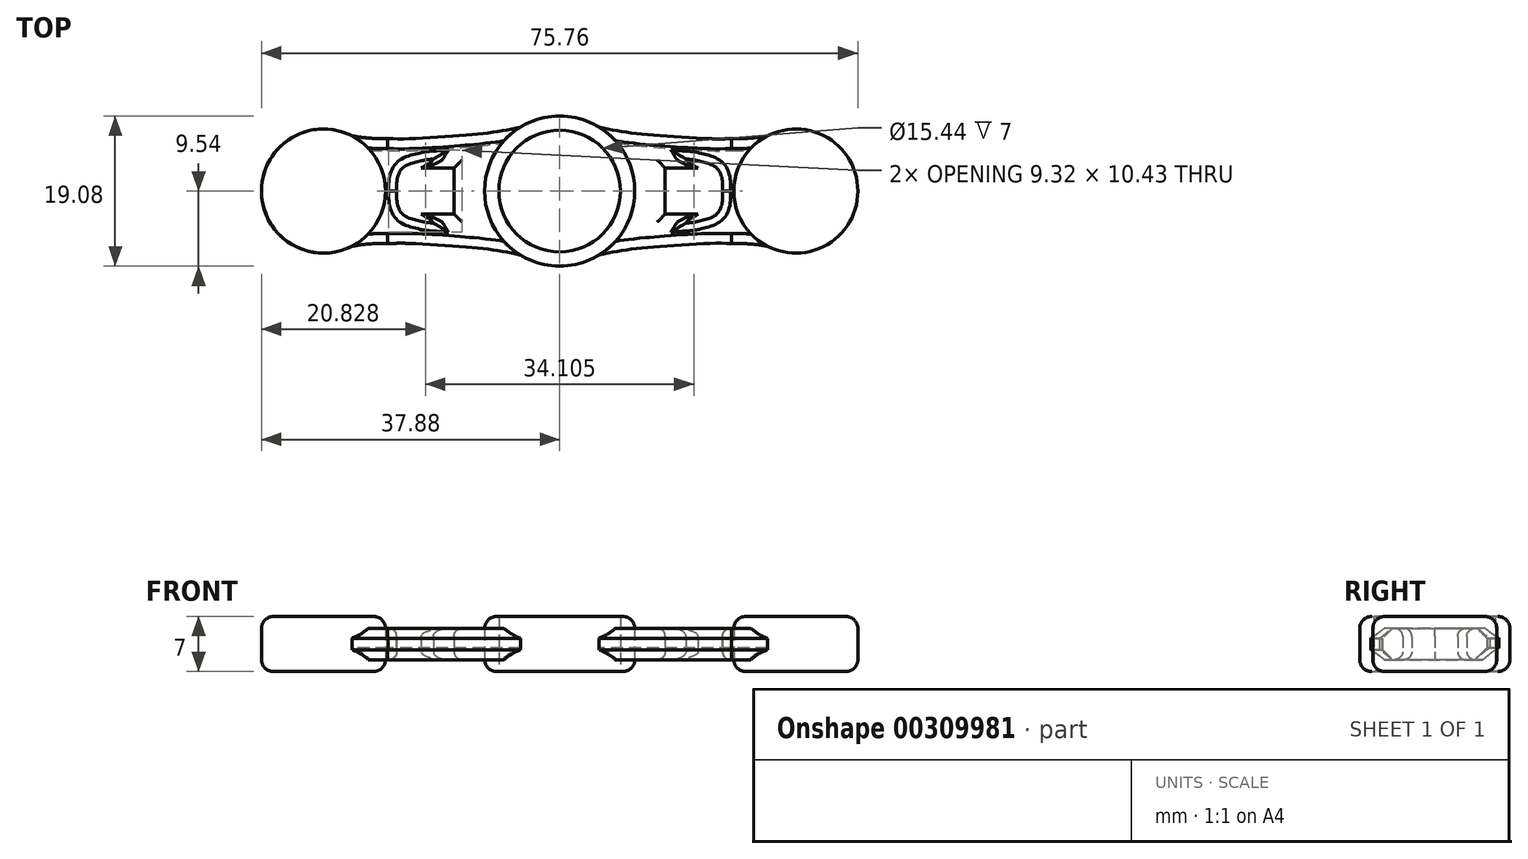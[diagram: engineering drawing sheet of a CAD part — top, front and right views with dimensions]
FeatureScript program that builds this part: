
annotation { "Feature Type Name" : "Feature", "Feature Type Description" : "" }
export const myFeature = defineFeature(function(context is Context, id is Id, definition is map)
    precondition{}
    {
        {
            var Q0;
            Q0=qCreatedBy(makeId("Top.planeOp"),FACE);
            var sketch = newSketch(context, id + "F0", { "sketchPlane" : qUnion([Q0])});
            skLineSegment(sketch, "E0.bottom", {"start": v(-38.2, 12.73) * mm, "end": v(38.2, 12.73) * mm});
            skLineSegment(sketch, "E0.top", {"start": v(-38.2, -12.73) * mm, "end": v(38.2, -12.73) * mm});
            skLineSegment(sketch, "E0.left", {"start": v(-38.2, 12.73) * mm, "end": v(-38.2, -12.73) * mm});
            skLineSegment(sketch, "E0.right", {"start": v(38.2, 12.73) * mm, "end": v(38.2, -12.73) * mm});
            skPoint(sketch, "E0.middle", {"position": v(0, 0) * mm});
            skCircle(sketch, "E1", {"center": v(0, 0) * mm, "radius": 7.72 * mm});
            skLineSegment(sketch, "E2", {"start": v(0, 12.73) * mm, "end": v(0, -12.73) * mm});
            skCircle(sketch, "E3", {"center": v(0, 0) * mm, "radius": 9.54 * mm});
            skFitSpline(sketch, "E4", {"points": [v(4.98, 8.14) * mm, v(7.16, 7.67) * mm, v(9.55, 7.33) * mm, v(13.3, 7) * mm, v(18.75, 6.65) * mm, v(21.82, 6.65) * mm], "startDerivative": vector(13.26, -2.94) * mm, "endDerivative": vector(14.49, 0.3) * mm});
            skFitSpline(sketch, "E5.MirrorCS", {"points": [v(4.98, -8.14) * mm, v(7.16, -7.67) * mm, v(9.55, -7.33) * mm, v(13.3, -7) * mm, v(18.75, -6.65) * mm, v(21.82, -6.65) * mm], "startDerivative": vector(13.26, 2.94) * mm, "endDerivative": vector(14.49, -0.3) * mm});
            skFitSpline(sketch, "E6.MirrorCS", {"points": [v(-4.98, 8.14) * mm, v(-7.16, 7.67) * mm, v(-9.55, 7.33) * mm, v(-13.3, 7) * mm, v(-18.75, 6.65) * mm, v(-21.82, 6.65) * mm], "startDerivative": vector(-13.26, -2.94) * mm, "endDerivative": vector(-14.49, 0.3) * mm});
            skFitSpline(sketch, "E7.MirrorCS", {"points": [v(-4.98, -8.14) * mm, v(-7.16, -7.67) * mm, v(-9.55, -7.33) * mm, v(-13.3, -7) * mm, v(-18.75, -6.65) * mm, v(-21.82, -6.65) * mm], "startDerivative": vector(-13.26, 2.94) * mm, "endDerivative": vector(-14.49, -0.3) * mm});
            skCircle(sketch, "E8", {"center": v(30, 0) * mm, "radius": 7.88 * mm});
            skLineSegment(sketch, "E9", {"start": v(38.2, 0) * mm, "end": v(-38.2, 0) * mm});
            skFitSpline(sketch, "E10", {"points": [v(21.82, 6.65) * mm, v(23.45, 6.68) * mm, v(25.2, 6.82) * mm, v(26.4, 7.01) * mm], "startDerivative": vector(4.61, 0.02) * mm, "endDerivative": vector(3.82, 0.64) * mm});
            skFitSpline(sketch, "E11.MirrorCS", {"points": [v(21.82, -6.65) * mm, v(23.45, -6.68) * mm, v(25.2, -6.82) * mm, v(26.4, -7.01) * mm], "startDerivative": vector(4.61, -0.02) * mm, "endDerivative": vector(3.82, -0.64) * mm});
            skCircle(sketch, "E12.MirrorC", {"center": v(-30, 0) * mm, "radius": 7.88 * mm});
            skFitSpline(sketch, "E13.MirrorCS", {"points": [v(-21.82, 6.65) * mm, v(-23.45, 6.68) * mm, v(-25.2, 6.82) * mm, v(-26.4, 7.01) * mm], "startDerivative": vector(-4.61, 0.02) * mm, "endDerivative": vector(-3.82, 0.64) * mm});
            skFitSpline(sketch, "E14.MirrorCS", {"points": [v(-21.82, -6.65) * mm, v(-23.45, -6.68) * mm, v(-25.2, -6.82) * mm, v(-26.4, -7.01) * mm], "startDerivative": vector(-4.61, -0.02) * mm, "endDerivative": vector(-3.82, -0.64) * mm});
            skFitSpline(sketch, "E15", {"points": [v(-20.68, 0) * mm, v(-20.68, 1.18) * mm, v(-20.38, 2.35) * mm, v(-19.72, 3.1) * mm, v(-18.7, 3.56) * mm, v(-17.5, 3.87) * mm], "startDerivative": vector(-0.27, 5.77) * mm, "endDerivative": vector(5.92, 1.32) * mm});
            skFitSpline(sketch, "E16", {"points": [v(-17.5, 3.87) * mm, v(-16.82, 4) * mm, v(-16.04, 4.07) * mm], "startDerivative": vector(1.36, 0.3) * mm, "endDerivative": vector(1.55, 0.1) * mm});
            skFitSpline(sketch, "E17", {"points": [v(-16.04, 4.07) * mm, v(-16.29, 3.75) * mm, v(-16.93, 3.32) * mm, v(-17.58, 2.92) * mm], "startDerivative": vector(-0.75, -1.2) * mm, "endDerivative": vector(-1.72, -1.06) * mm});
            skLineSegment(sketch, "E18", {"start": v(-17.58, 2.92) * mm, "end": v(-15.4, 2.92) * mm});
            skLineSegment(sketch, "E19.MirrorCS", {"start": v(-17.58, -2.92) * mm, "end": v(-15.4, -2.92) * mm});
            skFitSpline(sketch, "E20.MirrorCS", {"points": [v(-20.68, 0) * mm, v(-20.68, -1.18) * mm, v(-20.38, -2.35) * mm, v(-19.72, -3.1) * mm, v(-18.7, -3.56) * mm, v(-17.5, -3.87) * mm], "startDerivative": vector(-0.27, -5.77) * mm, "endDerivative": vector(5.92, -1.32) * mm});
            skFitSpline(sketch, "E21.MirrorCS", {"points": [v(-16.04, -4.07) * mm, v(-16.29, -3.75) * mm, v(-16.93, -3.32) * mm, v(-17.58, -2.92) * mm], "startDerivative": vector(-0.75, 1.2) * mm, "endDerivative": vector(-1.72, 1.06) * mm});
            skFitSpline(sketch, "E22.MirrorCS", {"points": [v(-17.5, -3.87) * mm, v(-16.82, -4) * mm, v(-16.04, -4.07) * mm], "startDerivative": vector(1.36, -0.3) * mm, "endDerivative": vector(1.55, -0.1) * mm});
            skFitSpline(sketch, "E23.MirrorCS", {"points": [v(20.68, 0) * mm, v(20.68, 1.18) * mm, v(20.38, 2.35) * mm, v(19.72, 3.1) * mm, v(18.7, 3.56) * mm, v(17.5, 3.87) * mm], "startDerivative": vector(0.27, 5.77) * mm, "endDerivative": vector(-5.92, 1.32) * mm});
            skFitSpline(sketch, "E24.MirrorCS", {"points": [v(17.5, 3.87) * mm, v(16.82, 4) * mm, v(16.04, 4.07) * mm], "startDerivative": vector(-1.36, 0.3) * mm, "endDerivative": vector(-1.55, 0.1) * mm});
            skFitSpline(sketch, "E25.MirrorCS", {"points": [v(16.04, 4.07) * mm, v(16.29, 3.75) * mm, v(16.93, 3.32) * mm, v(17.58, 2.92) * mm], "startDerivative": vector(0.75, -1.2) * mm, "endDerivative": vector(1.72, -1.06) * mm});
            skLineSegment(sketch, "E26.MirrorCS", {"start": v(17.58, 2.92) * mm, "end": v(15.4, 2.92) * mm});
            skLineSegment(sketch, "E27.MirrorCS", {"start": v(17.58, -2.92) * mm, "end": v(15.4, -2.92) * mm});
            skFitSpline(sketch, "E28.MirrorCS", {"points": [v(16.04, -4.07) * mm, v(16.29, -3.75) * mm, v(16.93, -3.32) * mm, v(17.58, -2.92) * mm], "startDerivative": vector(0.75, 1.2) * mm, "endDerivative": vector(1.72, 1.06) * mm});
            skFitSpline(sketch, "E29.MirrorCS", {"points": [v(17.5, -3.87) * mm, v(16.82, -4) * mm, v(16.04, -4.07) * mm], "startDerivative": vector(-1.36, -0.3) * mm, "endDerivative": vector(-1.55, -0.1) * mm});
            skFitSpline(sketch, "E30.MirrorCS", {"points": [v(20.68, 0) * mm, v(20.68, -1.18) * mm, v(20.38, -2.35) * mm, v(19.72, -3.1) * mm, v(18.7, -3.56) * mm, v(17.5, -3.87) * mm], "startDerivative": vector(0.27, -5.77) * mm, "endDerivative": vector(-5.92, -1.32) * mm});
            skLineSegment(sketch, "E31", {"start": v(-15.4, 2.92) * mm, "end": v(-13.4, 2.92) * mm});
            skLineSegment(sketch, "E32", {"start": v(-13.4, 2.92) * mm, "end": v(-13.4, 0) * mm});
            skLineSegment(sketch, "E33.MirrorCS", {"start": v(-13.4, -2.92) * mm, "end": v(-13.4, 0) * mm});
            skLineSegment(sketch, "E34.MirrorCS", {"start": v(-15.4, -2.92) * mm, "end": v(-13.4, -2.92) * mm});
            skLineSegment(sketch, "E35.MirrorCS", {"start": v(15.4, 2.92) * mm, "end": v(13.4, 2.92) * mm});
            skLineSegment(sketch, "E36.MirrorCS", {"start": v(13.4, 2.92) * mm, "end": v(13.4, 0) * mm});
            skLineSegment(sketch, "E37.MirrorCS", {"start": v(13.4, -2.92) * mm, "end": v(13.4, 0) * mm});
            skLineSegment(sketch, "E38.MirrorCS", {"start": v(15.4, -2.92) * mm, "end": v(13.4, -2.92) * mm});
            skSolve(sketch);
        }
        {
            var Q0;
            {var subQ0=sQuery(id+"F0.wireOp",EDGE,"E12.MirrorC");var subQ1=sQuery(id+"F0.wireOp",EDGE,"E9");var subQ2=makeQuery(id+"F0.imprint","INTERSECT",VERTEX,{"disambiguationData":[OD(0.0)],"derivedFrom":[subQ1,subQ0]});Q0=makeQuery(id+"F0.imprint","IMPRINT",FACE,{"disambiguationData":[TD([[makeQuery(id+"F0.imprint","IMPRINT",EDGE,{"disambiguationData":[TD([[subQ2,-1.0]])],"derivedFrom":subQ1}),-1.0]])]});}
            var Q1;
            {var subQ0=sQuery(id+"F0.wireOp",EDGE,"E12.MirrorC");var subQ1=sQuery(id+"F0.wireOp",EDGE,"E9");var subQ2=makeQuery(id+"F0.imprint","INTERSECT",VERTEX,{"disambiguationData":[OD(0.0)],"derivedFrom":[subQ1,subQ0]});Q1=makeQuery(id+"F0.imprint","IMPRINT",FACE,{"disambiguationData":[TD([[makeQuery(id+"F0.imprint","IMPRINT",EDGE,{"disambiguationData":[TD([[subQ2,-1.0]])],"derivedFrom":subQ1}),1.0]])]});}
            var Q2;
            {var subQ4=sQuery(id+"F0.wireOp",EDGE,"E9");var subQ6=sQuery(id+"F0.wireOp",EDGE,"E1");var subQ8=makeQuery(id+"F0.imprint","INTERSECT",VERTEX,{"disambiguationData":[OD(1.0)],"derivedFrom":[subQ6,subQ4]});Q2=makeQuery(id+"F0.imprint","IMPRINT",FACE,{"disambiguationData":[TD([[makeQuery(id+"F0.imprint","IMPRINT",EDGE,{"disambiguationData":[TD([[subQ8,-1.0]])],"derivedFrom":subQ6}),-1.0]])]});}
            var Q3;
            {var subQ4=sQuery(id+"F0.wireOp",EDGE,"E2");var subQ6=sQuery(id+"F0.wireOp",EDGE,"E1");var subQ7=makeQuery(id+"F0.imprint","INTERSECT",VERTEX,{"disambiguationData":[OD(0.0)],"derivedFrom":[subQ6,subQ4]});Q3=makeQuery(id+"F0.imprint","IMPRINT",FACE,{"disambiguationData":[TD([[makeQuery(id+"F0.imprint","IMPRINT",EDGE,{"disambiguationData":[TD([[subQ7,-1.0]])],"derivedFrom":subQ6}),-1.0]])]});}
            var Q4;
            {var subQ2=sQuery(id+"F0.wireOp",EDGE,"E2");var subQ4=sQuery(id+"F0.wireOp",EDGE,"E1");var subQ5=makeQuery(id+"F0.imprint","INTERSECT",VERTEX,{"disambiguationData":[OD(0.0)],"derivedFrom":[subQ4,subQ2]});Q4=makeQuery(id+"F0.imprint","IMPRINT",FACE,{"disambiguationData":[TD([[makeQuery(id+"F0.imprint","IMPRINT",EDGE,{"disambiguationData":[TD([[subQ5,1.0]])],"derivedFrom":subQ4}),-1.0]])]});}
            var Q5;
            {var subQ2=sQuery(id+"F0.wireOp",EDGE,"E9");var subQ6=sQuery(id+"F0.wireOp",EDGE,"E1");var subQ8=makeQuery(id+"F0.imprint","INTERSECT",VERTEX,{"disambiguationData":[OD(0.0)],"derivedFrom":[subQ6,subQ2]});Q5=makeQuery(id+"F0.imprint","IMPRINT",FACE,{"disambiguationData":[TD([[makeQuery(id+"F0.imprint","IMPRINT",EDGE,{"disambiguationData":[TD([[subQ8,1.0]])],"derivedFrom":subQ6}),-1.0]])]});}
            var Q6;
            {var subQ0=sQuery(id+"F0.wireOp",EDGE,"E8");var subQ1=makeQuery(id+"F0.imprint","INTERSECT",VERTEX,{"derivedFrom":[subQ0,sQuery(id+"F0.wireOp",EDGE,"E11.MirrorCS")]});Q6=makeQuery(id+"F0.imprint","IMPRINT",FACE,{"disambiguationData":[TD([[makeQuery(id+"F0.imprint","IMPRINT",EDGE,{"disambiguationData":[TD([[subQ1,1.0]])],"derivedFrom":subQ0}),1.0]])]});}
            var Q7;
            {var subQ0=sQuery(id+"F0.wireOp",EDGE,"E8");var subQ1=makeQuery(id+"F0.imprint","INTERSECT",VERTEX,{"derivedFrom":[subQ0,sQuery(id+"F0.wireOp",EDGE,"E10")]});Q7=makeQuery(id+"F0.imprint","IMPRINT",FACE,{"disambiguationData":[TD([[makeQuery(id+"F0.imprint","IMPRINT",EDGE,{"disambiguationData":[TD([[subQ1,1.0]])],"derivedFrom":subQ0}),1.0]])]});}
            extrude(context, id + "F1", {"entities" : qUnion([Q0, Q1, Q2, Q3, Q4, Q5, Q6, Q7]), "depth" : 7 * mm});
        }
        {
            var Q0;
            {var subQ4=sQuery(id+"F0.wireOp",EDGE,"E6.MirrorCS");Q0=makeQuery(id+"F0.imprint","IMPRINT",FACE,{"disambiguationData":[TD([[makeQuery(id+"F0.imprint","IMPRINT",EDGE,{"derivedFrom":subQ4}),1.0]])]});}
            var Q1;
            {var subQ5=sQuery(id+"F0.wireOp",EDGE,"E7.MirrorCS");Q1=makeQuery(id+"F0.imprint","IMPRINT",FACE,{"disambiguationData":[TD([[makeQuery(id+"F0.imprint","IMPRINT",EDGE,{"derivedFrom":subQ5}),-1.0]])]});}
            var Q2;
            {var subQ1=sQuery(id+"F0.wireOp",EDGE,"E5.MirrorCS");Q2=makeQuery(id+"F0.imprint","IMPRINT",FACE,{"disambiguationData":[TD([[makeQuery(id+"F0.imprint","IMPRINT",EDGE,{"derivedFrom":subQ1}),1.0]])]});}
            var Q3;
            {var subQ4=sQuery(id+"F0.wireOp",EDGE,"E4");Q3=makeQuery(id+"F0.imprint","IMPRINT",FACE,{"disambiguationData":[TD([[makeQuery(id+"F0.imprint","IMPRINT",EDGE,{"derivedFrom":subQ4}),-1.0]])]});}
            extrude(context, id + "F2", {"entities" : qUnion([Q0, Q1, Q2, Q3]), "depth" : 4 * mm});
        }
        {
            var Q0;
            Q0=makeQuery(id+"F2.opExtrude","SWEPT_BODY",BODY,{"disambiguationData":[OSD([sQuery(id+"F0.wireOp",EDGE,"E3"),sQuery(id+"F0.wireOp",EDGE,"E6.MirrorCS"),sQuery(id+"F0.wireOp",EDGE,"E7.MirrorCS"),sQuery(id+"F0.wireOp",EDGE,"E12.MirrorC"),sQuery(id+"F0.wireOp",EDGE,"E13.MirrorCS"),sQuery(id+"F0.wireOp",EDGE,"E14.MirrorCS"),sQuery(id+"F0.wireOp",EDGE,"E15"),sQuery(id+"F0.wireOp",EDGE,"E16"),sQuery(id+"F0.wireOp",EDGE,"E17"),sQuery(id+"F0.wireOp",EDGE,"E18"),sQuery(id+"F0.wireOp",EDGE,"E19.MirrorCS"),sQuery(id+"F0.wireOp",EDGE,"E20.MirrorCS"),sQuery(id+"F0.wireOp",EDGE,"E21.MirrorCS"),sQuery(id+"F0.wireOp",EDGE,"E22.MirrorCS"),sQuery(id+"F0.wireOp",EDGE,"E31"),sQuery(id+"F0.wireOp",EDGE,"E32"),sQuery(id+"F0.wireOp",EDGE,"E33.MirrorCS"),sQuery(id+"F0.wireOp",EDGE,"E34.MirrorCS")])]});
            transform(context, id + "F3", {"entities" : qUnion([Q0]), "transformType" : TransformType.TRANSLATION_3D, "dx" : 0 * mm, "dy" : 0 * mm, "dz" : 1 * mm, "makeCopy" : false});
        }
        {
            var Q0;
            Q0=makeQuery(id+"F2.opExtrude","SWEPT_BODY",BODY,{"disambiguationData":[OSD([sQuery(id+"F0.wireOp",EDGE,"E3"),sQuery(id+"F0.wireOp",EDGE,"E4"),sQuery(id+"F0.wireOp",EDGE,"E5.MirrorCS"),sQuery(id+"F0.wireOp",EDGE,"E8"),sQuery(id+"F0.wireOp",EDGE,"E10"),sQuery(id+"F0.wireOp",EDGE,"E11.MirrorCS"),sQuery(id+"F0.wireOp",EDGE,"E23.MirrorCS"),sQuery(id+"F0.wireOp",EDGE,"E24.MirrorCS"),sQuery(id+"F0.wireOp",EDGE,"E25.MirrorCS"),sQuery(id+"F0.wireOp",EDGE,"E26.MirrorCS"),sQuery(id+"F0.wireOp",EDGE,"E27.MirrorCS"),sQuery(id+"F0.wireOp",EDGE,"E28.MirrorCS"),sQuery(id+"F0.wireOp",EDGE,"E29.MirrorCS"),sQuery(id+"F0.wireOp",EDGE,"E30.MirrorCS"),sQuery(id+"F0.wireOp",EDGE,"E35.MirrorCS"),sQuery(id+"F0.wireOp",EDGE,"E36.MirrorCS"),sQuery(id+"F0.wireOp",EDGE,"E37.MirrorCS"),sQuery(id+"F0.wireOp",EDGE,"E38.MirrorCS")])]});
            transform(context, id + "F4", {"entities" : qUnion([Q0]), "transformType" : TransformType.TRANSLATION_3D, "dx" : 0 * mm, "dy" : 0 * mm, "dz" : 1 * mm, "makeCopy" : false});
        }
        {
            var Q0;
            Q0=makeQuery(id+"F2.opExtrude","SWEPT_BODY",BODY,{"disambiguationData":[OSD([sQuery(id+"F0.wireOp",EDGE,"E3"),sQuery(id+"F0.wireOp",EDGE,"E6.MirrorCS"),sQuery(id+"F0.wireOp",EDGE,"E7.MirrorCS"),sQuery(id+"F0.wireOp",EDGE,"E12.MirrorC"),sQuery(id+"F0.wireOp",EDGE,"E13.MirrorCS"),sQuery(id+"F0.wireOp",EDGE,"E14.MirrorCS"),sQuery(id+"F0.wireOp",EDGE,"E15"),sQuery(id+"F0.wireOp",EDGE,"E16"),sQuery(id+"F0.wireOp",EDGE,"E17"),sQuery(id+"F0.wireOp",EDGE,"E18"),sQuery(id+"F0.wireOp",EDGE,"E19.MirrorCS"),sQuery(id+"F0.wireOp",EDGE,"E20.MirrorCS"),sQuery(id+"F0.wireOp",EDGE,"E21.MirrorCS"),sQuery(id+"F0.wireOp",EDGE,"E22.MirrorCS"),sQuery(id+"F0.wireOp",EDGE,"E31"),sQuery(id+"F0.wireOp",EDGE,"E32"),sQuery(id+"F0.wireOp",EDGE,"E33.MirrorCS"),sQuery(id+"F0.wireOp",EDGE,"E34.MirrorCS")])]});
            transform(context, id + "F5", {"entities" : qUnion([Q0]), "transformType" : TransformType.TRANSLATION_3D, "dx" : 0 * mm, "dy" : 0 * mm, "dz" : -1 * mm, "makeCopy" : false});
        }
        {
            var Q0;
            Q0=makeQuery(id+"F2.opExtrude","SWEPT_BODY",BODY,{"disambiguationData":[OSD([sQuery(id+"F0.wireOp",EDGE,"E3"),sQuery(id+"F0.wireOp",EDGE,"E4"),sQuery(id+"F0.wireOp",EDGE,"E5.MirrorCS"),sQuery(id+"F0.wireOp",EDGE,"E8"),sQuery(id+"F0.wireOp",EDGE,"E10"),sQuery(id+"F0.wireOp",EDGE,"E11.MirrorCS"),sQuery(id+"F0.wireOp",EDGE,"E23.MirrorCS"),sQuery(id+"F0.wireOp",EDGE,"E24.MirrorCS"),sQuery(id+"F0.wireOp",EDGE,"E25.MirrorCS"),sQuery(id+"F0.wireOp",EDGE,"E26.MirrorCS"),sQuery(id+"F0.wireOp",EDGE,"E27.MirrorCS"),sQuery(id+"F0.wireOp",EDGE,"E28.MirrorCS"),sQuery(id+"F0.wireOp",EDGE,"E29.MirrorCS"),sQuery(id+"F0.wireOp",EDGE,"E30.MirrorCS"),sQuery(id+"F0.wireOp",EDGE,"E35.MirrorCS"),sQuery(id+"F0.wireOp",EDGE,"E36.MirrorCS"),sQuery(id+"F0.wireOp",EDGE,"E37.MirrorCS"),sQuery(id+"F0.wireOp",EDGE,"E38.MirrorCS")])]});
            transform(context, id + "F6", {"entities" : qUnion([Q0]), "transformType" : TransformType.TRANSLATION_3D, "dx" : 0 * mm, "dy" : 0 * mm, "dz" : -1 * mm, "makeCopy" : false});
        }
        {
            var Q0;
            Q0=makeQuery(id+"F2.opExtrude","SWEPT_BODY",BODY,{"disambiguationData":[OSD([sQuery(id+"F0.wireOp",EDGE,"E3"),sQuery(id+"F0.wireOp",EDGE,"E6.MirrorCS"),sQuery(id+"F0.wireOp",EDGE,"E7.MirrorCS"),sQuery(id+"F0.wireOp",EDGE,"E12.MirrorC"),sQuery(id+"F0.wireOp",EDGE,"E13.MirrorCS"),sQuery(id+"F0.wireOp",EDGE,"E14.MirrorCS"),sQuery(id+"F0.wireOp",EDGE,"E15"),sQuery(id+"F0.wireOp",EDGE,"E16"),sQuery(id+"F0.wireOp",EDGE,"E17"),sQuery(id+"F0.wireOp",EDGE,"E18"),sQuery(id+"F0.wireOp",EDGE,"E19.MirrorCS"),sQuery(id+"F0.wireOp",EDGE,"E20.MirrorCS"),sQuery(id+"F0.wireOp",EDGE,"E21.MirrorCS"),sQuery(id+"F0.wireOp",EDGE,"E22.MirrorCS"),sQuery(id+"F0.wireOp",EDGE,"E31"),sQuery(id+"F0.wireOp",EDGE,"E32"),sQuery(id+"F0.wireOp",EDGE,"E33.MirrorCS"),sQuery(id+"F0.wireOp",EDGE,"E34.MirrorCS")])]});
            var Q1;
            Q1=makeQuery(id+"F2.opExtrude","SWEPT_BODY",BODY,{"disambiguationData":[OSD([sQuery(id+"F0.wireOp",EDGE,"E3"),sQuery(id+"F0.wireOp",EDGE,"E4"),sQuery(id+"F0.wireOp",EDGE,"E5.MirrorCS"),sQuery(id+"F0.wireOp",EDGE,"E8"),sQuery(id+"F0.wireOp",EDGE,"E10"),sQuery(id+"F0.wireOp",EDGE,"E11.MirrorCS"),sQuery(id+"F0.wireOp",EDGE,"E23.MirrorCS"),sQuery(id+"F0.wireOp",EDGE,"E24.MirrorCS"),sQuery(id+"F0.wireOp",EDGE,"E25.MirrorCS"),sQuery(id+"F0.wireOp",EDGE,"E26.MirrorCS"),sQuery(id+"F0.wireOp",EDGE,"E27.MirrorCS"),sQuery(id+"F0.wireOp",EDGE,"E28.MirrorCS"),sQuery(id+"F0.wireOp",EDGE,"E29.MirrorCS"),sQuery(id+"F0.wireOp",EDGE,"E30.MirrorCS"),sQuery(id+"F0.wireOp",EDGE,"E35.MirrorCS"),sQuery(id+"F0.wireOp",EDGE,"E36.MirrorCS"),sQuery(id+"F0.wireOp",EDGE,"E37.MirrorCS"),sQuery(id+"F0.wireOp",EDGE,"E38.MirrorCS")])]});
            transform(context, id + "F7", {"entities" : qUnion([Q0, Q1]), "transformType" : TransformType.TRANSLATION_3D, "dx" : 0 * mm, "dy" : 0 * mm, "dz" : 1.5 * mm, "makeCopy" : false});
        }
        {
            var Q0;
            Q0=makeQuery(id+"F2.opExtrude","CAP_EDGE",EDGE,{"disambiguationData":[OSD([sQuery(id+"F0.wireOp",EDGE,"E7.MirrorCS")])],"isStart":false});
            var Q1;
            Q1=makeQuery(id+"F2.opExtrude","CAP_EDGE",EDGE,{"disambiguationData":[OSD([sQuery(id+"F0.wireOp",EDGE,"E14.MirrorCS")])],"isStart":false});
            chamfer(context, id + "F8", {"entities" : qUnion([Q0, Q1]), "width" : 1.27 * mm, "tangentPropagation" : true});
        }
        {
            var Q0;
            Q0=makeQuery(id+"F2.opExtrude","CAP_EDGE",EDGE,{"disambiguationData":[OSD([sQuery(id+"F0.wireOp",EDGE,"E5.MirrorCS")])],"isStart":false});
            var Q1;
            Q1=makeQuery(id+"F2.opExtrude","CAP_EDGE",EDGE,{"disambiguationData":[OSD([sQuery(id+"F0.wireOp",EDGE,"E11.MirrorCS")])],"isStart":false});
            chamfer(context, id + "F9", {"entities" : qUnion([Q0, Q1]), "width" : 1.27 * mm, "tangentPropagation" : true});
        }
        {
            var Q0;
            Q0=makeQuery(id+"F2.opExtrude","CAP_EDGE",EDGE,{"disambiguationData":[OSD([sQuery(id+"F0.wireOp",EDGE,"E6.MirrorCS")])],"isStart":false});
            var Q1;
            Q1=makeQuery(id+"F2.opExtrude","CAP_EDGE",EDGE,{"disambiguationData":[OSD([sQuery(id+"F0.wireOp",EDGE,"E13.MirrorCS")])],"isStart":false});
            chamfer(context, id + "F10", {"entities" : qUnion([Q0, Q1]), "width" : 1.27 * mm, "tangentPropagation" : true});
        }
        {
            var Q0;
            Q0=makeQuery(id+"F2.opExtrude","CAP_EDGE",EDGE,{"disambiguationData":[OSD([sQuery(id+"F0.wireOp",EDGE,"E4")])],"isStart":false});
            var Q1;
            Q1=makeQuery(id+"F2.opExtrude","CAP_EDGE",EDGE,{"disambiguationData":[OSD([sQuery(id+"F0.wireOp",EDGE,"E10")])],"isStart":false});
            chamfer(context, id + "F11", {"entities" : qUnion([Q0, Q1]), "width" : 1.27 * mm, "tangentPropagation" : true});
        }
        {
            var Q0;
            Q0=makeQuery(id+"F2.opExtrude","CAP_EDGE",EDGE,{"disambiguationData":[OSD([sQuery(id+"F0.wireOp",EDGE,"E7.MirrorCS")])],"isStart":true});
            var Q1;
            Q1=makeQuery(id+"F2.opExtrude","CAP_EDGE",EDGE,{"disambiguationData":[OSD([sQuery(id+"F0.wireOp",EDGE,"E14.MirrorCS")])],"isStart":true});
            chamfer(context, id + "F12", {"entities" : qUnion([Q0, Q1]), "width" : 1.27 * mm, "tangentPropagation" : true});
        }
        {
            var Q0;
            Q0=makeQuery(id+"F2.opExtrude","CAP_EDGE",EDGE,{"disambiguationData":[OSD([sQuery(id+"F0.wireOp",EDGE,"E5.MirrorCS")])],"isStart":true});
            var Q1;
            Q1=makeQuery(id+"F2.opExtrude","CAP_EDGE",EDGE,{"disambiguationData":[OSD([sQuery(id+"F0.wireOp",EDGE,"E11.MirrorCS")])],"isStart":true});
            chamfer(context, id + "F13", {"entities" : qUnion([Q0, Q1]), "width" : 1.27 * mm, "tangentPropagation" : true});
        }
        {
            var Q0;
            Q0=makeQuery(id+"F1.opExtrude","CAP_EDGE",EDGE,{"disambiguationData":[OSD([sQuery(id+"F0.wireOp",EDGE,"E8")])],"isStart":false});
            fillet(context, id + "F14", {"entities" : qUnion([Q0]), "radius" : 1.52 * mm, "tangentPropagation" : true, "allowEdgeOverflow" : false});
        }
        {
            var Q0;
            Q0=makeQuery(id+"F1.opExtrude","CAP_EDGE",EDGE,{"disambiguationData":[OSD([sQuery(id+"F0.wireOp",EDGE,"E12.MirrorC")])],"isStart":false});
            fillet(context, id + "F15", {"entities" : qUnion([Q0]), "radius" : 1.52 * mm, "tangentPropagation" : true, "allowEdgeOverflow" : false});
        }
        {
            var Q0;
            Q0=makeQuery(id+"F1.opExtrude","SWEPT_BODY",BODY,{"disambiguationData":[OSD([sQuery(id+"F0.wireOp",EDGE,"E8")])]});
            transform(context, id + "F16", {"entities" : qUnion([Q0]), "transformType" : TransformType.TRANSLATION_3D, "dx" : 0 * mm, "dy" : 0 * mm, "dz" : 1 * mm, "makeCopy" : false});
        }
        {
            var Q0;
            Q0=makeQuery(id+"F2.opExtrude","SWEPT_BODY",BODY,{"disambiguationData":[OSD([sQuery(id+"F0.wireOp",EDGE,"E3"),sQuery(id+"F0.wireOp",EDGE,"E4"),sQuery(id+"F0.wireOp",EDGE,"E5.MirrorCS"),sQuery(id+"F0.wireOp",EDGE,"E8"),sQuery(id+"F0.wireOp",EDGE,"E10"),sQuery(id+"F0.wireOp",EDGE,"E11.MirrorCS"),sQuery(id+"F0.wireOp",EDGE,"E23.MirrorCS"),sQuery(id+"F0.wireOp",EDGE,"E24.MirrorCS"),sQuery(id+"F0.wireOp",EDGE,"E25.MirrorCS"),sQuery(id+"F0.wireOp",EDGE,"E26.MirrorCS"),sQuery(id+"F0.wireOp",EDGE,"E27.MirrorCS"),sQuery(id+"F0.wireOp",EDGE,"E28.MirrorCS"),sQuery(id+"F0.wireOp",EDGE,"E29.MirrorCS"),sQuery(id+"F0.wireOp",EDGE,"E30.MirrorCS"),sQuery(id+"F0.wireOp",EDGE,"E35.MirrorCS"),sQuery(id+"F0.wireOp",EDGE,"E36.MirrorCS"),sQuery(id+"F0.wireOp",EDGE,"E37.MirrorCS"),sQuery(id+"F0.wireOp",EDGE,"E38.MirrorCS")])]});
            transform(context, id + "F17", {"entities" : qUnion([Q0]), "transformType" : TransformType.TRANSLATION_3D, "dx" : 0 * mm, "dy" : 0 * mm, "dz" : 1 * mm, "makeCopy" : false});
        }
        {
            var Q0;
            Q0=makeQuery(id+"F1.opExtrude","SWEPT_BODY",BODY,{"disambiguationData":[OSD([sQuery(id+"F0.wireOp",EDGE,"E1"),sQuery(id+"F0.wireOp",EDGE,"E3")])]});
            transform(context, id + "F18", {"entities" : qUnion([Q0]), "transformType" : TransformType.TRANSLATION_3D, "dx" : 0 * mm, "dy" : 0 * mm, "dz" : 1 * mm, "makeCopy" : false});
        }
        {
            var Q0;
            Q0=makeQuery(id+"F2.opExtrude","SWEPT_BODY",BODY,{"disambiguationData":[OSD([sQuery(id+"F0.wireOp",EDGE,"E3"),sQuery(id+"F0.wireOp",EDGE,"E6.MirrorCS"),sQuery(id+"F0.wireOp",EDGE,"E7.MirrorCS"),sQuery(id+"F0.wireOp",EDGE,"E12.MirrorC"),sQuery(id+"F0.wireOp",EDGE,"E13.MirrorCS"),sQuery(id+"F0.wireOp",EDGE,"E14.MirrorCS"),sQuery(id+"F0.wireOp",EDGE,"E15"),sQuery(id+"F0.wireOp",EDGE,"E16"),sQuery(id+"F0.wireOp",EDGE,"E17"),sQuery(id+"F0.wireOp",EDGE,"E18"),sQuery(id+"F0.wireOp",EDGE,"E19.MirrorCS"),sQuery(id+"F0.wireOp",EDGE,"E20.MirrorCS"),sQuery(id+"F0.wireOp",EDGE,"E21.MirrorCS"),sQuery(id+"F0.wireOp",EDGE,"E22.MirrorCS"),sQuery(id+"F0.wireOp",EDGE,"E31"),sQuery(id+"F0.wireOp",EDGE,"E32"),sQuery(id+"F0.wireOp",EDGE,"E33.MirrorCS"),sQuery(id+"F0.wireOp",EDGE,"E34.MirrorCS")])]});
            transform(context, id + "F19", {"entities" : qUnion([Q0]), "transformType" : TransformType.TRANSLATION_3D, "dx" : 0 * mm, "dy" : 0 * mm, "dz" : 1 * mm, "makeCopy" : false});
        }
        {
            var Q0;
            Q0=makeQuery(id+"F1.opExtrude","SWEPT_BODY",BODY,{"disambiguationData":[OSD([sQuery(id+"F0.wireOp",EDGE,"E12.MirrorC")])]});
            transform(context, id + "F20", {"entities" : qUnion([Q0]), "transformType" : TransformType.TRANSLATION_3D, "dx" : 0 * mm, "dy" : 0 * mm, "dz" : 1 * mm, "makeCopy" : false});
        }
        {
            var Q0;
            Q0=makeQuery(id+"F1.opExtrude","CAP_EDGE",EDGE,{"disambiguationData":[OSD([sQuery(id+"F0.wireOp",EDGE,"E8")])],"isStart":true});
            fillet(context, id + "F21", {"entities" : qUnion([Q0]), "radius" : 1.52 * mm, "tangentPropagation" : true, "allowEdgeOverflow" : false});
        }
        {
            var Q0;
            Q0=makeQuery(id+"F1.opExtrude","CAP_EDGE",EDGE,{"disambiguationData":[OSD([sQuery(id+"F0.wireOp",EDGE,"E3")])],"isStart":true});
            fillet(context, id + "F22", {"entities" : qUnion([Q0]), "radius" : 1.52 * mm, "tangentPropagation" : true, "allowEdgeOverflow" : false});
        }
        {
            var Q0;
            Q0=makeQuery(id+"F1.opExtrude","CAP_EDGE",EDGE,{"disambiguationData":[OSD([sQuery(id+"F0.wireOp",EDGE,"E12.MirrorC")])],"isStart":true});
            fillet(context, id + "F23", {"entities" : qUnion([Q0]), "radius" : 1.52 * mm, "tangentPropagation" : true, "allowEdgeOverflow" : false});
        }
        {
            var Q0;
            Q0=makeQuery(id+"F1.opExtrude","CAP_EDGE",EDGE,{"disambiguationData":[OSD([sQuery(id+"F0.wireOp",EDGE,"E3")])],"isStart":false});
            fillet(context, id + "F24", {"entities" : qUnion([Q0]), "radius" : 1.52 * mm, "tangentPropagation" : true, "allowEdgeOverflow" : false});
        }
        {
            var Q0;
            Q0=makeQuery(id+"F1.opExtrude","SWEPT_BODY",BODY,{"disambiguationData":[OSD([sQuery(id+"F0.wireOp",EDGE,"E8")])]});
            transform(context, id + "F25", {"entities" : qUnion([Q0]), "transformType" : TransformType.TRANSLATION_3D, "dx" : 0 * mm, "dy" : 0 * mm, "dz" : -1 * mm, "makeCopy" : false});
        }
        {
            var Q0;
            Q0=makeQuery(id+"F1.opExtrude","SWEPT_BODY",BODY,{"disambiguationData":[OSD([sQuery(id+"F0.wireOp",EDGE,"E1"),sQuery(id+"F0.wireOp",EDGE,"E3")])]});
            transform(context, id + "F26", {"entities" : qUnion([Q0]), "transformType" : TransformType.TRANSLATION_3D, "dx" : 0 * mm, "dy" : 0 * mm, "dz" : -1 * mm, "makeCopy" : false});
        }
        {
            var Q0;
            Q0=makeQuery(id+"F2.opExtrude","SWEPT_BODY",BODY,{"disambiguationData":[OSD([sQuery(id+"F0.wireOp",EDGE,"E3"),sQuery(id+"F0.wireOp",EDGE,"E6.MirrorCS"),sQuery(id+"F0.wireOp",EDGE,"E7.MirrorCS"),sQuery(id+"F0.wireOp",EDGE,"E12.MirrorC"),sQuery(id+"F0.wireOp",EDGE,"E13.MirrorCS"),sQuery(id+"F0.wireOp",EDGE,"E14.MirrorCS"),sQuery(id+"F0.wireOp",EDGE,"E15"),sQuery(id+"F0.wireOp",EDGE,"E16"),sQuery(id+"F0.wireOp",EDGE,"E17"),sQuery(id+"F0.wireOp",EDGE,"E18"),sQuery(id+"F0.wireOp",EDGE,"E19.MirrorCS"),sQuery(id+"F0.wireOp",EDGE,"E20.MirrorCS"),sQuery(id+"F0.wireOp",EDGE,"E21.MirrorCS"),sQuery(id+"F0.wireOp",EDGE,"E22.MirrorCS"),sQuery(id+"F0.wireOp",EDGE,"E31"),sQuery(id+"F0.wireOp",EDGE,"E32"),sQuery(id+"F0.wireOp",EDGE,"E33.MirrorCS"),sQuery(id+"F0.wireOp",EDGE,"E34.MirrorCS")])]});
            transform(context, id + "F27", {"entities" : qUnion([Q0]), "transformType" : TransformType.TRANSLATION_3D, "dx" : 0 * mm, "dy" : 0 * mm, "dz" : -1 * mm, "makeCopy" : false});
        }
        {
            var Q0;
            Q0=makeQuery(id+"F1.opExtrude","SWEPT_BODY",BODY,{"disambiguationData":[OSD([sQuery(id+"F0.wireOp",EDGE,"E12.MirrorC")])]});
            transform(context, id + "F28", {"entities" : qUnion([Q0]), "transformType" : TransformType.TRANSLATION_3D, "dx" : 0 * mm, "dy" : 0 * mm, "dz" : -1 * mm, "makeCopy" : false});
        }
        {
            var Q0;
            Q0=makeQuery(id+"F2.opExtrude","CAP_EDGE",EDGE,{"disambiguationData":[OSD([sQuery(id+"F0.wireOp",EDGE,"E18"),sQuery(id+"F0.wireOp",EDGE,"E31")])],"isStart":false});
            var Q1;
            Q1=makeQuery(id+"F2.opExtrude","CAP_EDGE",EDGE,{"disambiguationData":[OSD([sQuery(id+"F0.wireOp",EDGE,"E17")])],"isStart":false});
            var Q2;
            Q2=makeQuery(id+"F2.opExtrude","CAP_EDGE",EDGE,{"disambiguationData":[OSD([sQuery(id+"F0.wireOp",EDGE,"E16")])],"isStart":false});
            var Q3;
            Q3=makeQuery(id+"F2.opExtrude","CAP_EDGE",EDGE,{"disambiguationData":[OSD([sQuery(id+"F0.wireOp",EDGE,"E15")])],"isStart":false});
            var Q4;
            Q4=makeQuery(id+"F2.opExtrude","CAP_EDGE",EDGE,{"disambiguationData":[OSD([sQuery(id+"F0.wireOp",EDGE,"E20.MirrorCS")])],"isStart":false});
            var Q5;
            Q5=makeQuery(id+"F2.opExtrude","CAP_EDGE",EDGE,{"disambiguationData":[OSD([sQuery(id+"F0.wireOp",EDGE,"E21.MirrorCS")])],"isStart":false});
            var Q6;
            Q6=makeQuery(id+"F2.opExtrude","CAP_EDGE",EDGE,{"disambiguationData":[OSD([sQuery(id+"F0.wireOp",EDGE,"E22.MirrorCS")])],"isStart":false});
            var Q7;
            Q7=makeQuery(id+"F2.opExtrude","CAP_EDGE",EDGE,{"disambiguationData":[OSD([sQuery(id+"F0.wireOp",EDGE,"E19.MirrorCS"),sQuery(id+"F0.wireOp",EDGE,"E34.MirrorCS")])],"isStart":false});
            var Q8;
            Q8=makeQuery(id+"F2.opExtrude","CAP_EDGE",EDGE,{"disambiguationData":[OSD([sQuery(id+"F0.wireOp",EDGE,"E32"),sQuery(id+"F0.wireOp",EDGE,"E33.MirrorCS")])],"isStart":false});
            fillet(context, id + "F29", {"entities" : qUnion([Q0, Q1, Q2, Q3, Q4, Q5, Q6, Q7, Q8]), "radius" : 1.02 * mm, "tangentPropagation" : true, "allowEdgeOverflow" : false});
        }
        {
            var Q0;
            Q0=makeQuery(id+"F2.opExtrude","CAP_EDGE",EDGE,{"disambiguationData":[OSD([sQuery(id+"F0.wireOp",EDGE,"E26.MirrorCS"),sQuery(id+"F0.wireOp",EDGE,"E35.MirrorCS")])],"isStart":false});
            var Q1;
            Q1=makeQuery(id+"F2.opExtrude","CAP_EDGE",EDGE,{"disambiguationData":[OSD([sQuery(id+"F0.wireOp",EDGE,"E24.MirrorCS")])],"isStart":false});
            var Q2;
            Q2=makeQuery(id+"F2.opExtrude","CAP_EDGE",EDGE,{"disambiguationData":[OSD([sQuery(id+"F0.wireOp",EDGE,"E25.MirrorCS")])],"isStart":false});
            var Q3;
            Q3=makeQuery(id+"F2.opExtrude","CAP_EDGE",EDGE,{"disambiguationData":[OSD([sQuery(id+"F0.wireOp",EDGE,"E23.MirrorCS")])],"isStart":false});
            var Q4;
            Q4=makeQuery(id+"F2.opExtrude","CAP_EDGE",EDGE,{"disambiguationData":[OSD([sQuery(id+"F0.wireOp",EDGE,"E30.MirrorCS")])],"isStart":false});
            var Q5;
            Q5=makeQuery(id+"F2.opExtrude","CAP_EDGE",EDGE,{"disambiguationData":[OSD([sQuery(id+"F0.wireOp",EDGE,"E29.MirrorCS")])],"isStart":false});
            var Q6;
            Q6=makeQuery(id+"F2.opExtrude","CAP_EDGE",EDGE,{"disambiguationData":[OSD([sQuery(id+"F0.wireOp",EDGE,"E28.MirrorCS")])],"isStart":false});
            var Q7;
            Q7=makeQuery(id+"F2.opExtrude","CAP_EDGE",EDGE,{"disambiguationData":[OSD([sQuery(id+"F0.wireOp",EDGE,"E27.MirrorCS"),sQuery(id+"F0.wireOp",EDGE,"E38.MirrorCS")])],"isStart":false});
            var Q8;
            Q8=makeQuery(id+"F2.opExtrude","CAP_EDGE",EDGE,{"disambiguationData":[OSD([sQuery(id+"F0.wireOp",EDGE,"E36.MirrorCS"),sQuery(id+"F0.wireOp",EDGE,"E37.MirrorCS")])],"isStart":false});
            fillet(context, id + "F30", {"entities" : qUnion([Q0, Q1, Q2, Q3, Q4, Q5, Q6, Q7, Q8]), "radius" : 1.02 * mm, "tangentPropagation" : true, "allowEdgeOverflow" : false});
        }
        {
            var Q0;
            Q0=makeQuery(id+"F2.opExtrude","CAP_EDGE",EDGE,{"disambiguationData":[OSD([sQuery(id+"F0.wireOp",EDGE,"E27.MirrorCS"),sQuery(id+"F0.wireOp",EDGE,"E38.MirrorCS")])],"isStart":true});
            var Q1;
            Q1=makeQuery(id+"F2.opExtrude","CAP_EDGE",EDGE,{"disambiguationData":[OSD([sQuery(id+"F0.wireOp",EDGE,"E29.MirrorCS")])],"isStart":true});
            var Q2;
            Q2=makeQuery(id+"F2.opExtrude","CAP_EDGE",EDGE,{"disambiguationData":[OSD([sQuery(id+"F0.wireOp",EDGE,"E28.MirrorCS")])],"isStart":true});
            var Q3;
            Q3=makeQuery(id+"F2.opExtrude","CAP_EDGE",EDGE,{"disambiguationData":[OSD([sQuery(id+"F0.wireOp",EDGE,"E30.MirrorCS")])],"isStart":true});
            var Q4;
            Q4=makeQuery(id+"F2.opExtrude","CAP_EDGE",EDGE,{"disambiguationData":[OSD([sQuery(id+"F0.wireOp",EDGE,"E36.MirrorCS"),sQuery(id+"F0.wireOp",EDGE,"E37.MirrorCS")])],"isStart":true});
            var Q5;
            Q5=makeQuery(id+"F2.opExtrude","CAP_EDGE",EDGE,{"disambiguationData":[OSD([sQuery(id+"F0.wireOp",EDGE,"E26.MirrorCS"),sQuery(id+"F0.wireOp",EDGE,"E35.MirrorCS")])],"isStart":true});
            var Q6;
            Q6=makeQuery(id+"F2.opExtrude","CAP_EDGE",EDGE,{"disambiguationData":[OSD([sQuery(id+"F0.wireOp",EDGE,"E25.MirrorCS")])],"isStart":true});
            var Q7;
            Q7=makeQuery(id+"F2.opExtrude","CAP_EDGE",EDGE,{"disambiguationData":[OSD([sQuery(id+"F0.wireOp",EDGE,"E23.MirrorCS")])],"isStart":true});
            var Q8;
            Q8=makeQuery(id+"F2.opExtrude","CAP_EDGE",EDGE,{"disambiguationData":[OSD([sQuery(id+"F0.wireOp",EDGE,"E24.MirrorCS")])],"isStart":true});
            fillet(context, id + "F31", {"entities" : qUnion([Q0, Q1, Q2, Q3, Q4, Q5, Q6, Q7, Q8]), "radius" : 1.02 * mm, "tangentPropagation" : true, "allowEdgeOverflow" : false});
        }
        {
            var Q0;
            Q0=makeQuery(id+"F2.opExtrude","CAP_EDGE",EDGE,{"disambiguationData":[OSD([sQuery(id+"F0.wireOp",EDGE,"E19.MirrorCS"),sQuery(id+"F0.wireOp",EDGE,"E34.MirrorCS")])],"isStart":true});
            var Q1;
            Q1=makeQuery(id+"F2.opExtrude","CAP_EDGE",EDGE,{"disambiguationData":[OSD([sQuery(id+"F0.wireOp",EDGE,"E22.MirrorCS")])],"isStart":true});
            var Q2;
            Q2=makeQuery(id+"F2.opExtrude","CAP_EDGE",EDGE,{"disambiguationData":[OSD([sQuery(id+"F0.wireOp",EDGE,"E21.MirrorCS")])],"isStart":true});
            var Q3;
            Q3=makeQuery(id+"F2.opExtrude","CAP_EDGE",EDGE,{"disambiguationData":[OSD([sQuery(id+"F0.wireOp",EDGE,"E20.MirrorCS")])],"isStart":true});
            var Q4;
            Q4=makeQuery(id+"F2.opExtrude","CAP_EDGE",EDGE,{"disambiguationData":[OSD([sQuery(id+"F0.wireOp",EDGE,"E15")])],"isStart":true});
            var Q5;
            Q5=makeQuery(id+"F2.opExtrude","CAP_EDGE",EDGE,{"disambiguationData":[OSD([sQuery(id+"F0.wireOp",EDGE,"E17")])],"isStart":true});
            var Q6;
            Q6=makeQuery(id+"F2.opExtrude","CAP_EDGE",EDGE,{"disambiguationData":[OSD([sQuery(id+"F0.wireOp",EDGE,"E16")])],"isStart":true});
            var Q7;
            Q7=makeQuery(id+"F2.opExtrude","CAP_EDGE",EDGE,{"disambiguationData":[OSD([sQuery(id+"F0.wireOp",EDGE,"E18"),sQuery(id+"F0.wireOp",EDGE,"E31")])],"isStart":true});
            var Q8;
            Q8=makeQuery(id+"F2.opExtrude","CAP_EDGE",EDGE,{"disambiguationData":[OSD([sQuery(id+"F0.wireOp",EDGE,"E32"),sQuery(id+"F0.wireOp",EDGE,"E33.MirrorCS")])],"isStart":true});
            fillet(context, id + "F32", {"entities" : qUnion([Q0, Q1, Q2, Q3, Q4, Q5, Q6, Q7, Q8]), "radius" : 1.02 * mm, "tangentPropagation" : true, "allowEdgeOverflow" : false});
        }
        {
            var Q0;
            Q0=makeQuery(id+"F2.opExtrude","SWEPT_BODY",BODY,{"disambiguationData":[OSD([sQuery(id+"F0.wireOp",EDGE,"E3"),sQuery(id+"F0.wireOp",EDGE,"E4"),sQuery(id+"F0.wireOp",EDGE,"E5.MirrorCS"),sQuery(id+"F0.wireOp",EDGE,"E8"),sQuery(id+"F0.wireOp",EDGE,"E10"),sQuery(id+"F0.wireOp",EDGE,"E11.MirrorCS"),sQuery(id+"F0.wireOp",EDGE,"E23.MirrorCS"),sQuery(id+"F0.wireOp",EDGE,"E24.MirrorCS"),sQuery(id+"F0.wireOp",EDGE,"E25.MirrorCS"),sQuery(id+"F0.wireOp",EDGE,"E26.MirrorCS"),sQuery(id+"F0.wireOp",EDGE,"E27.MirrorCS"),sQuery(id+"F0.wireOp",EDGE,"E28.MirrorCS"),sQuery(id+"F0.wireOp",EDGE,"E29.MirrorCS"),sQuery(id+"F0.wireOp",EDGE,"E30.MirrorCS"),sQuery(id+"F0.wireOp",EDGE,"E35.MirrorCS"),sQuery(id+"F0.wireOp",EDGE,"E36.MirrorCS"),sQuery(id+"F0.wireOp",EDGE,"E37.MirrorCS"),sQuery(id+"F0.wireOp",EDGE,"E38.MirrorCS")])]});
            transform(context, id + "F33", {"entities" : qUnion([Q0]), "transformType" : TransformType.TRANSLATION_3D, "dx" : 0 * mm, "dy" : 0 * mm, "dz" : -1 * mm, "makeCopy" : false});
        }
        {
            var Q0;
            Q0=makeQuery(id+"F2.opExtrude","CAP_EDGE",EDGE,{"disambiguationData":[OSD([sQuery(id+"F0.wireOp",EDGE,"E13.MirrorCS")])],"isStart":true});
            var Q1;
            Q1=makeQuery(id+"F2.opExtrude","CAP_EDGE",EDGE,{"disambiguationData":[OSD([sQuery(id+"F0.wireOp",EDGE,"E6.MirrorCS")])],"isStart":true});
            chamfer(context, id + "F34", {"entities" : qUnion([Q0, Q1]), "width" : 1.52 * mm, "tangentPropagation" : true});
        }
        {
            var Q0;
            Q0=makeQuery(id+"F2.opExtrude","CAP_EDGE",EDGE,{"disambiguationData":[OSD([sQuery(id+"F0.wireOp",EDGE,"E4")])],"isStart":true});
            var Q1;
            Q1=makeQuery(id+"F2.opExtrude","CAP_EDGE",EDGE,{"disambiguationData":[OSD([sQuery(id+"F0.wireOp",EDGE,"E10")])],"isStart":true});
            chamfer(context, id + "F35", {"entities" : qUnion([Q0, Q1]), "width" : 1.52 * mm, "tangentPropagation" : true});
        }
    });
